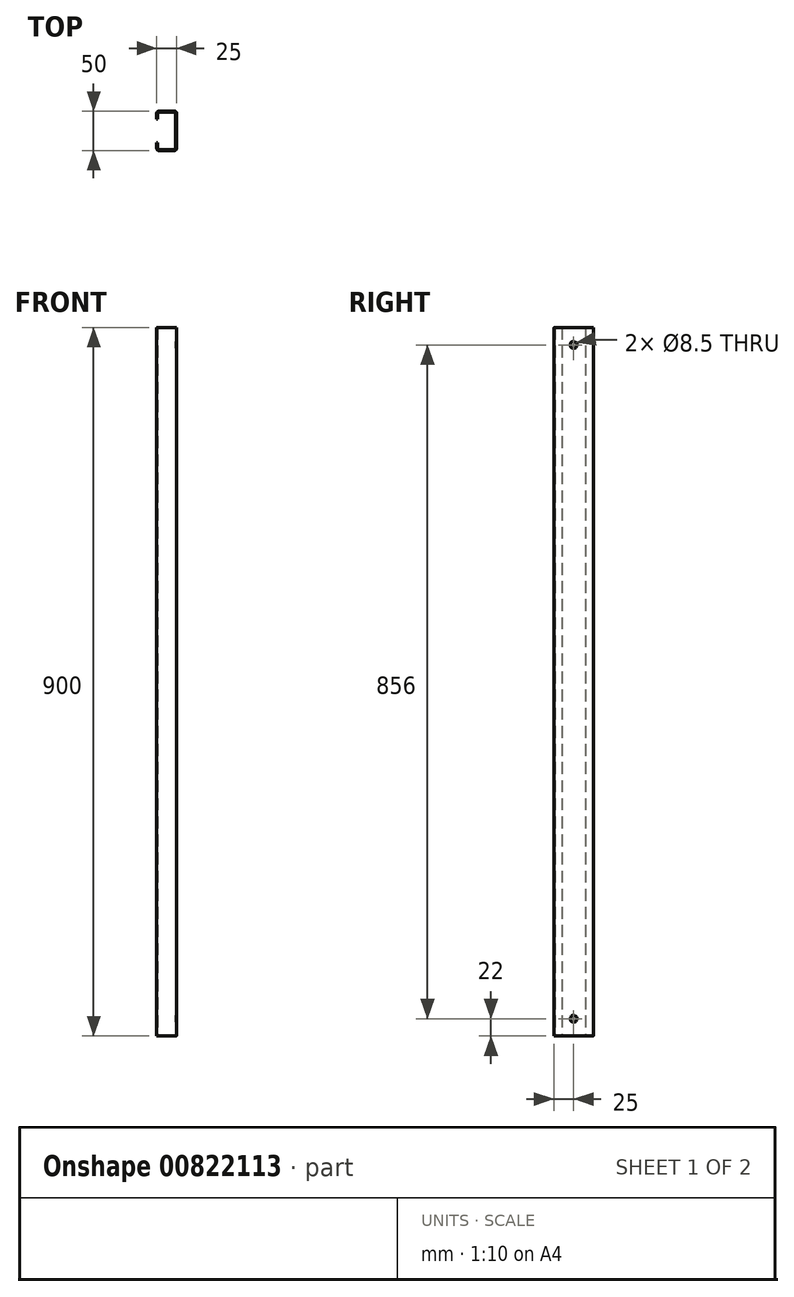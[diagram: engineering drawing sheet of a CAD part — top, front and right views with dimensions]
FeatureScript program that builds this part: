
annotation { "Feature Type Name" : "Feature", "Feature Type Description" : "" }
export const myFeature = defineFeature(function(context is Context, id is Id, definition is map)
    precondition{}
    {
        {
            var Q0;
            Q0=qCreatedBy(makeId("Top.planeOp"),FACE);
            var sketch = newSketch(context, id + "F0", { "sketchPlane" : qUnion([Q0])});
            skLineSegment(sketch, "E0", {"start": v(10, 25) * mm, "end": v(-10, 25) * mm});
            skArc(sketch, "E1", {"start": v(-10, 25) * mm, "mid": v(-11.77, 24.27) * mm, "end": v(-12.5, 22.5) * mm});
            skLineSegment(sketch, "E2", {"start": v(-12.5, 22.5) * mm, "end": v(-12.5, 15) * mm});
            skLineSegment(sketch, "E3", {"start": v(-12.5, 15) * mm, "end": v(-11.3, 15) * mm});
            skLineSegment(sketch, "E4", {"start": v(-11.3, 15) * mm, "end": v(-11.3, 22.5) * mm});
            skArc(sketch, "E5", {"start": v(-11.3, 22.5) * mm, "mid": v(-10.92, 23.42) * mm, "end": v(-10, 23.8) * mm});
            skLineSegment(sketch, "E6", {"start": v(-10, 23.8) * mm, "end": v(10, 23.8) * mm});
            skArc(sketch, "E7", {"start": v(10, 23.8) * mm, "mid": v(10.92, 23.42) * mm, "end": v(11.3, 22.5) * mm});
            skLineSegment(sketch, "E8", {"start": v(11.3, 22.5) * mm, "end": v(11.3, -22.5) * mm});
            skArc(sketch, "E9", {"start": v(11.3, -22.5) * mm, "mid": v(10.92, -23.42) * mm, "end": v(10, -23.8) * mm});
            skLineSegment(sketch, "E10", {"start": v(10, -23.8) * mm, "end": v(-10, -23.8) * mm});
            skArc(sketch, "E11", {"start": v(-10, -23.8) * mm, "mid": v(-10.92, -23.42) * mm, "end": v(-11.3, -22.5) * mm});
            skLineSegment(sketch, "E12", {"start": v(-11.3, -22.5) * mm, "end": v(-11.3, -15) * mm});
            skLineSegment(sketch, "E13", {"start": v(-11.3, -15) * mm, "end": v(-12.5, -15) * mm});
            skLineSegment(sketch, "E14", {"start": v(-12.5, -15) * mm, "end": v(-12.5, -22.5) * mm});
            skArc(sketch, "E15", {"start": v(-12.5, -22.5) * mm, "mid": v(-11.77, -24.27) * mm, "end": v(-10, -25) * mm});
            skLineSegment(sketch, "E16", {"start": v(-10, -25) * mm, "end": v(10, -25) * mm});
            skArc(sketch, "E17", {"start": v(10, -25) * mm, "mid": v(11.77, -24.27) * mm, "end": v(12.5, -22.5) * mm});
            skLineSegment(sketch, "E18", {"start": v(12.5, -22.5) * mm, "end": v(12.5, 22.5) * mm});
            skArc(sketch, "E19", {"start": v(12.5, 22.5) * mm, "mid": v(11.77, 24.27) * mm, "end": v(10, 25) * mm});
            skSolve(sketch);
        }
        {
            assignVariable(context, id + "F1", {"name" : "Longitud", "anyValue" : 900});
        }
        {
            var Q0;
            Q0=qSketchRegion(id+"F0",true);
            extrude(context, id + "F2", {"entities" : qUnion([Q0]), "depth" : (getVariable(context, 'Longitud')) * mm});
        }
        {
            var Q0;
            Q0=makeQuery(id+"F2.opExtrude","SWEPT_FACE",FACE,{"disambiguationData":[OSD([sQuery(id+"F0.wireOp",EDGE,"E18")])]});
            var sketch = newSketch(context, id + "F3", { "sketchPlane" : qUnion([Q0])});
            skCircle(sketch, "E20", {"center": v(0, 22) * mm, "radius": 4.25 * mm});
            skCircle(sketch, "E21", {"center": v(0, 878) * mm, "radius": 4.25 * mm});
            skSolve(sketch);
        }
        {
            var Q0;
            Q0=qSketchRegion(id+"F3",true);
            var Q1;
            Q1=makeQuery(id+"F2.opExtrude","SWEPT_FACE",FACE,{"disambiguationData":[OSD([sQuery(id+"F0.wireOp",EDGE,"E8")])]});
            extrude(context, id + "F4", {"entities" : qUnion([Q0]), "operationType" : NewBodyOperationType.REMOVE, "endBound" : BoundingType.UP_TO_SURFACE, "oppositeDirection" : true, "endBoundEntityFace" : qUnion([Q1]), "depth" : 25 * mm});
        }
    });
